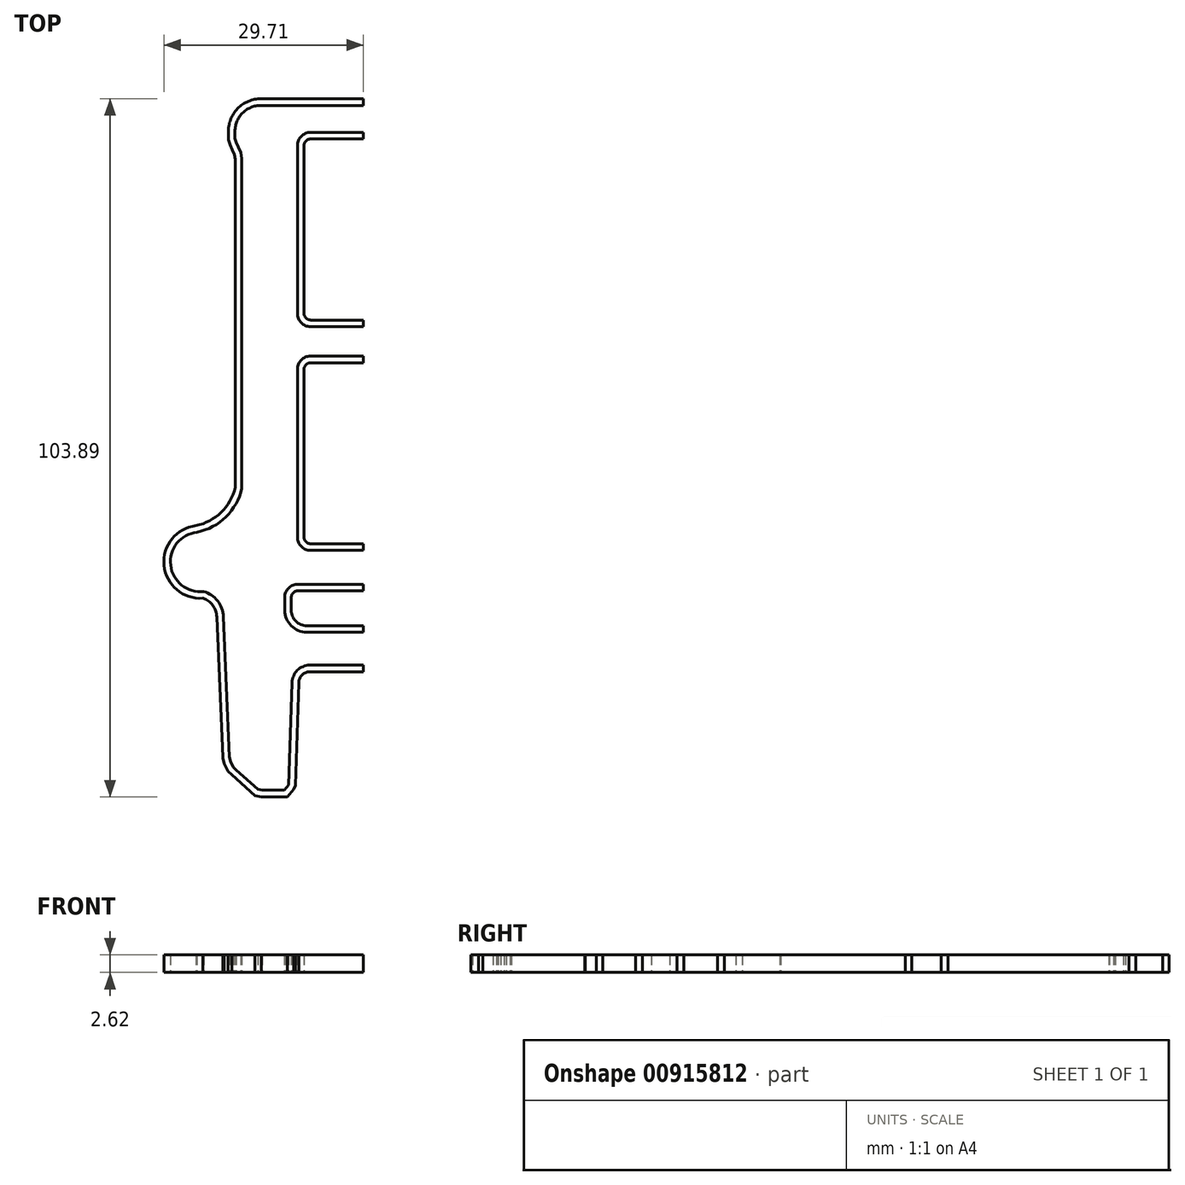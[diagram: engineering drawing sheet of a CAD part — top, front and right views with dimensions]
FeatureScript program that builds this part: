
annotation { "Feature Type Name" : "Feature", "Feature Type Description" : "" }
export const myFeature = defineFeature(function(context is Context, id is Id, definition is map)
    precondition{}
    {
        {
            var Q0;
            Q0=qCreatedBy(makeId("Top.planeOp"),FACE);
            var sketch = newSketch(context, id + "F0", { "sketchPlane" : qUnion([Q0])});
            skLineSegment(sketch, "E0.left", {"start": v(-27.58, 80.06) * mm, "end": v(-27.58, -59.75) * mm});
            skLineSegment(sketch, "E1.bottom", {"start": v(-11.99, 35.27) * mm, "end": v(0, 35.27) * mm});
            skLineSegment(sketch, "E1.top", {"start": v(-11.99, -8.8) * mm, "end": v(0, -8.8) * mm});
            skLineSegment(sketch, "E1.left", {"start": v(-14.99, 32.27) * mm, "end": v(-14.99, -5.8) * mm});
            skPoint(sketch, "E2.visualSharp", {"position": v(-14.99, 36.07) * mm});
            skArc(sketch, "E2.filletArc", {"start": v(-11.99, 35.27) * mm, "mid": v(-14.1, 34.39) * mm, "end": v(-14.99, 32.27) * mm});
            skPoint(sketch, "E3.visualSharp", {"position": v(-14.99, -8.8) * mm});
            skArc(sketch, "E3.filletArc", {"start": v(-14.99, -5.8) * mm, "mid": v(-14.1, -7.92) * mm, "end": v(-11.99, -8.8) * mm});
            skLineSegment(sketch, "E4.bottom", {"start": v(-11.99, 86.01) * mm, "end": v(0, 86.01) * mm});
            skLineSegment(sketch, "E4.top", {"start": v(-11.99, 41.94) * mm, "end": v(0, 41.94) * mm});
            skLineSegment(sketch, "E4.left", {"start": v(-14.99, 83.01) * mm, "end": v(-14.99, 44.94) * mm});
            skPoint(sketch, "E5.visualSharp", {"position": v(-14.99, 86.01) * mm});
            skArc(sketch, "E5.filletArc", {"start": v(-11.99, 86.01) * mm, "mid": v(-14.1, 85.13) * mm, "end": v(-14.99, 83.01) * mm});
            skPoint(sketch, "E6.visualSharp", {"position": v(-14.99, 41.94) * mm});
            skArc(sketch, "E6.filletArc", {"start": v(-14.99, 44.94) * mm, "mid": v(-14.1, 42.82) * mm, "end": v(-11.99, 41.94) * mm});
            skLineSegment(sketch, "E7.bottom", {"start": v(-12.87, -27.38) * mm, "end": v(0, -27.38) * mm});
            skLineSegment(sketch, "E7.top", {"start": v(-14.87, -16.48) * mm, "end": v(0, -16.48) * mm});
            skLineSegment(sketch, "E7.left", {"start": v(-17.87, -22.38) * mm, "end": v(-17.87, -19.48) * mm});
            skPoint(sketch, "E8.visualSharp", {"position": v(-17.87, -16.48) * mm});
            skArc(sketch, "E8.filletArc", {"start": v(-14.87, -16.48) * mm, "mid": v(-16.99, -17.36) * mm, "end": v(-17.87, -19.48) * mm});
            skPoint(sketch, "E9.visualSharp", {"position": v(-17.87, -27.38) * mm});
            skArc(sketch, "E9.filletArc", {"start": v(-17.87, -22.38) * mm, "mid": v(-16.4, -25.92) * mm, "end": v(-12.87, -27.38) * mm});
            skLineSegment(sketch, "E10.bottom", {"start": v(-12.18, -34.84) * mm, "end": v(0, -34.84) * mm});
            skPoint(sketch, "E11.visualSharp", {"position": v(-16.18, -34.84) * mm});
            skArc(sketch, "E11.filletArc", {"start": v(-12.18, -34.84) * mm, "mid": v(-15, -36.01) * mm, "end": v(-16.18, -38.84) * mm});
            skLineSegment(sketch, "E12", {"start": v(-16.18, -38.84) * mm, "end": v(-16.96, -62.01) * mm});
            skLineSegment(sketch, "E13", {"start": v(-16.96, -62.01) * mm, "end": v(-17.99, -63.22) * mm});
            skLineSegment(sketch, "E14", {"start": v(-17.99, -63.22) * mm, "end": v(-23, -63.22) * mm});
            skLineSegment(sketch, "E15", {"start": v(-23, -63.22) * mm, "end": v(-23.9, -63.02) * mm});
            skLineSegment(sketch, "E16", {"start": v(-23.9, -63.02) * mm, "end": v(-28.85, -58.61) * mm});
            skCircle(sketch, "E17", {"center": v(-23.01, -55.13) * mm, "radius": 2.4 * mm});
            skCircle(sketch, "E18", {"center": v(-37, -11.4) * mm, "radius": 6.78 * mm});
            skCircle(sketch, "E19", {"center": v(-37, -11.4) * mm, "radius": 2.4 * mm});
            skLineSegment(sketch, "E20", {"start": v(-31.78, -23.86) * mm, "end": v(-30.39, -55.6) * mm});
            skLineSegment(sketch, "E21", {"start": v(-30.39, -55.6) * mm, "end": v(-30.18, -56.73) * mm});
            skLineSegment(sketch, "E22", {"start": v(-30.18, -56.73) * mm, "end": v(-29.54, -57.98) * mm});
            skLineSegment(sketch, "E23", {"start": v(-29.54, -57.98) * mm, "end": v(-28.85, -58.61) * mm});
            skArc(sketch, "E24", {"start": v(-31.78, -23.86) * mm, "mid": v(-33.08, -20.26) * mm, "end": v(-36.27, -18.14) * mm});
            skArc(sketch, "E25", {"start": v(-37.75, -4.67) * mm, "mid": v(-31.18, -1.2) * mm, "end": v(-27.58, 5.3) * mm});
            skCircle(sketch, "E26", {"center": v(-23.25, 86.23) * mm, "radius": 2.4 * mm});
            skCircle(sketch, "E27", {"center": v(-23.25, 86.23) * mm, "radius": 5.9 * mm});
            skLineSegment(sketch, "E28", {"start": v(-29.15, 86) * mm, "end": v(-29.15, 84.6) * mm});
            skLineSegment(sketch, "E29", {"start": v(-29.15, 84.6) * mm, "end": v(-28.88, 83.73) * mm});
            skLineSegment(sketch, "E30", {"start": v(-28.88, 83.73) * mm, "end": v(-28.4, 82.67) * mm});
            skLineSegment(sketch, "E31", {"start": v(-28.4, 82.67) * mm, "end": v(-27.86, 81.45) * mm});
            skLineSegment(sketch, "E32", {"start": v(-27.86, 81.45) * mm, "end": v(-27.58, 80.06) * mm});
            skLineSegment(sketch, "E33", {"start": v(-23.2, 92.14) * mm, "end": v(0, 92.14) * mm});
            skLineSegment(sketch, "E34.right", {"start": v(0, 92.14) * mm, "end": v(0, 86.01) * mm});
            skLineSegment(sketch, "E35.trimOffspring", {"start": v(0, 41.94) * mm, "end": v(0, 35.27) * mm});
            skLineSegment(sketch, "E36.trimOffspring", {"start": v(0, -8.8) * mm, "end": v(0, -16.48) * mm});
            skLineSegment(sketch, "E37.trimOffspring", {"start": v(0, -27.38) * mm, "end": v(0, -34.84) * mm});
            skLineSegment(sketch, "E38.0", {"start": v(-23.2, 93.64) * mm, "end": v(0, 93.64) * mm});
            skCircle(sketch, "E39.0", {"center": v(-37, -11.4) * mm, "radius": 8.28 * mm});
            skArc(sketch, "E40.0", {"start": v(-38.04, -3.2) * mm, "mid": v(-32.23, -0.12) * mm, "end": v(-29.04, 5.62) * mm});
            skLineSegment(sketch, "E41.0", {"start": v(-29.08, 80.06) * mm, "end": v(-29.08, -59.75) * mm});
            skLineSegment(sketch, "E42.0", {"start": v(-29.3, 80.98) * mm, "end": v(-29.05, 79.76) * mm});
            skLineSegment(sketch, "E42.1", {"start": v(-30.65, 86) * mm, "end": v(-30.65, 84.37) * mm});
            skLineSegment(sketch, "E42.2", {"start": v(-30.65, 84.37) * mm, "end": v(-30.29, 83.2) * mm});
            skLineSegment(sketch, "E42.3", {"start": v(-30.29, 83.2) * mm, "end": v(-29.78, 82.06) * mm});
            skLineSegment(sketch, "E42.4", {"start": v(-29.78, 82.06) * mm, "end": v(-29.3, 80.98) * mm});
            skCircle(sketch, "E43.0", {"center": v(-23.25, 86.23) * mm, "radius": 7.4 * mm});
            skLineSegment(sketch, "E44", {"start": v(0, 93.64) * mm, "end": v(0, 91.95) * mm});
            skLineSegment(sketch, "E45.0", {"start": v(-11.99, 84.51) * mm, "end": v(0, 84.51) * mm});
            skArc(sketch, "E46.0", {"start": v(-11.99, 84.51) * mm, "mid": v(-13.05, 84.07) * mm, "end": v(-13.49, 83.01) * mm});
            skLineSegment(sketch, "E47.0", {"start": v(-13.49, 83.01) * mm, "end": v(-13.49, 44.94) * mm});
            skArc(sketch, "E48.0", {"start": v(-13.49, 44.94) * mm, "mid": v(-13.05, 43.88) * mm, "end": v(-11.99, 43.44) * mm});
            skLineSegment(sketch, "E49.0", {"start": v(-11.99, 43.44) * mm, "end": v(0, 43.44) * mm});
            skLineSegment(sketch, "E50", {"start": v(0, 43.44) * mm, "end": v(0, 41.94) * mm});
            skLineSegment(sketch, "E51.0", {"start": v(-11.99, 33.77) * mm, "end": v(0, 33.77) * mm});
            skArc(sketch, "E52.0", {"start": v(-11.99, 33.77) * mm, "mid": v(-13.05, 33.33) * mm, "end": v(-13.49, 32.27) * mm});
            skLineSegment(sketch, "E53.0", {"start": v(-13.49, 32.27) * mm, "end": v(-13.49, -5.8) * mm});
            skLineSegment(sketch, "E54", {"start": v(0, 35.27) * mm, "end": v(0, 33.77) * mm});
            skArc(sketch, "E55.0", {"start": v(-13.49, -5.8) * mm, "mid": v(-13.05, -6.86) * mm, "end": v(-11.99, -7.3) * mm});
            skLineSegment(sketch, "E56.0", {"start": v(-11.99, -7.3) * mm, "end": v(0, -7.3) * mm});
            skLineSegment(sketch, "E57.0", {"start": v(-14.87, -17.98) * mm, "end": v(0, -17.98) * mm});
            skLineSegment(sketch, "E58", {"start": v(0, -7.3) * mm, "end": v(0, -17.98) * mm});
            skArc(sketch, "E59.0", {"start": v(-14.87, -17.98) * mm, "mid": v(-15.93, -18.42) * mm, "end": v(-16.37, -19.48) * mm});
            skLineSegment(sketch, "E60.0", {"start": v(-16.37, -22.38) * mm, "end": v(-16.37, -19.48) * mm});
            skArc(sketch, "E61.0", {"start": v(-16.37, -22.38) * mm, "mid": v(-15.34, -24.86) * mm, "end": v(-12.87, -25.88) * mm});
            skLineSegment(sketch, "E62.0", {"start": v(-12.87, -25.88) * mm, "end": v(0, -25.88) * mm});
            skLineSegment(sketch, "E63.0", {"start": v(-12.18, -36.34) * mm, "end": v(0, -36.34) * mm});
            skArc(sketch, "E64.0", {"start": v(-12.18, -36.34) * mm, "mid": v(-13.94, -37.07) * mm, "end": v(-14.68, -38.84) * mm});
            skLineSegment(sketch, "E65.0", {"start": v(-14.68, -38.9) * mm, "end": v(-15.46, -62.06) * mm});
            skLineSegment(sketch, "E66.0", {"start": v(-15.82, -62.98) * mm, "end": v(-17.3, -64.72) * mm});
            skLineSegment(sketch, "E66.1", {"start": v(-17.3, -64.72) * mm, "end": v(-23.17, -64.72) * mm});
            skLineSegment(sketch, "E66.2", {"start": v(-23.17, -64.72) * mm, "end": v(-24.61, -64.4) * mm});
            skLineSegment(sketch, "E66.3", {"start": v(-31.86, -55.88) * mm, "end": v(-31.62, -57.21) * mm});
            skLineSegment(sketch, "E66.4", {"start": v(-31.62, -57.21) * mm, "end": v(-30.75, -58.9) * mm});
            skLineSegment(sketch, "E66.5", {"start": v(-30.75, -58.9) * mm, "end": v(-29.85, -59.73) * mm});
            skLineSegment(sketch, "E66.6", {"start": v(-24.61, -64.4) * mm, "end": v(-29.85, -59.73) * mm});
            skLineSegment(sketch, "E67", {"start": v(-15.46, -62.06) * mm, "end": v(-15.82, -62.98) * mm});
            skLineSegment(sketch, "E68.0", {"start": v(-33.27, -23.92) * mm, "end": v(-31.88, -55.67) * mm});
            skLineSegment(sketch, "E69", {"start": v(-31.88, -55.67) * mm, "end": v(-31.86, -55.88) * mm});
            skArc(sketch, "E70.0", {"start": v(-33.27, -23.9) * mm, "mid": v(-34.19, -21.3) * mm, "end": v(-36.42, -19.66) * mm});
            skLineSegment(sketch, "E71", {"start": v(0, 86.01) * mm, "end": v(0, 84.51) * mm});
            skLineSegment(sketch, "E72", {"start": v(0, -25.88) * mm, "end": v(0, -36.34) * mm});
            skLineSegment(sketch, "E73", {"start": v(-14.68, -38.84) * mm, "end": v(-14.68, -38.9) * mm});
            skLineSegment(sketch, "E74", {"start": v(0, -34.84) * mm, "end": v(0, -36.34) * mm});
            skLineSegment(sketch, "E75", {"start": v(-33.27, -23.9) * mm, "end": v(-33.27, -23.92) * mm});
            skSolve(sketch);
        }
        {
            var Q0;
            Q0=makeQuery(id+"F0.imprint","IMPRINT",FACE,{"disambiguationData":[TD([[makeQuery(id+"F0.imprint","IMPRINT",EDGE,{"derivedFrom":sQuery(id+"F0.wireOp",EDGE,"E1.bottom")}),-1.0]])]});
            var Q1;
            {var subQ2=sQuery(id+"F0.wireOp",EDGE,"E7.bottom");Q1=makeQuery(id+"F0.imprint","IMPRINT",FACE,{"disambiguationData":[TD([[makeQuery(id+"F0.imprint","IMPRINT",EDGE,{"derivedFrom":subQ2}),1.0]])]});}
            var Q2;
            {var subQ5=sQuery(id+"F0.wireOp",EDGE,"E38.0");Q2=makeQuery(id+"F0.imprint","IMPRINT",FACE,{"disambiguationData":[TD([[makeQuery(id+"F0.imprint","IMPRINT",EDGE,{"derivedFrom":subQ5}),-1.0]])]});}
            var Q3;
            {var subQ0=sQuery(id+"F0.wireOp",EDGE,"E39.0");var subQ1=sQuery(id+"F0.wireOp",EDGE,"E25");var subQ2=makeQuery(id+"F0.imprint","INTERSECT",VERTEX,{"derivedFrom":[subQ1,subQ0]});Q3=makeQuery(id+"F0.imprint","IMPRINT",FACE,{"disambiguationData":[TD([[makeQuery(id+"F0.imprint","IMPRINT",EDGE,{"disambiguationData":[TD([[subQ2,-1.0]])],"derivedFrom":subQ1}),1.0]])]});}
            var Q4;
            {var subQ0=sQuery(id+"F0.wireOp",EDGE,"E42.2");Q4=makeQuery(id+"F0.imprint","IMPRINT",FACE,{"disambiguationData":[TD([[makeQuery(id+"F0.imprint","IMPRINT",EDGE,{"derivedFrom":subQ0}),1.0]])]});}
            var Q5;
            Q5=makeQuery(id+"F0.imprint","IMPRINT",FACE,{"disambiguationData":[TD([[makeQuery(id+"F0.imprint","IMPRINT",EDGE,{"derivedFrom":sQuery(id+"F0.wireOp",EDGE,"E10.bottom")}),-1.0]])]});
            var Q6;
            {var subQ4=sQuery(id+"F0.wireOp",EDGE,"E24");var subQ5=sQuery(id+"F0.wireOp",EDGE,"E18");var subQ6=makeQuery(id+"F0.imprint","INTERSECT",VERTEX,{"derivedFrom":[subQ5,subQ4]});Q6=makeQuery(id+"F0.imprint","IMPRINT",FACE,{"disambiguationData":[TD([[makeQuery(id+"F0.imprint","IMPRINT",EDGE,{"disambiguationData":[TD([[subQ6,1.0]])],"derivedFrom":subQ5}),-1.0]])]});}
            var Q7;
            {var subQ0=sQuery(id+"F0.wireOp",EDGE,"E28");Q7=makeQuery(id+"F0.imprint","IMPRINT",FACE,{"disambiguationData":[TD([[makeQuery(id+"F0.imprint","IMPRINT",EDGE,{"derivedFrom":subQ0}),-1.0]])]});}
            var Q8;
            Q8=makeQuery(id+"F0.imprint","IMPRINT",FACE,{"disambiguationData":[TD([[makeQuery(id+"F0.imprint","IMPRINT",EDGE,{"derivedFrom":sQuery(id+"F0.wireOp",EDGE,"E4.bottom")}),-1.0]])]});
            extrude(context, id + "F1", {"entities" : qUnion([Q0, Q1, Q2, Q3, Q4, Q5, Q6, Q7, Q8]), "depth" : 4 * mm, "offsetDistance" : 25 * mm});
        }
        {
            var Q0;
            Q0=makeQuery(id+"F1.opExtrude","SWEPT_BODY",BODY,{"disambiguationData":[OSD([sQuery(id+"F0.wireOp",EDGE,"E7.bottom"),sQuery(id+"F0.wireOp",EDGE,"E7.top"),sQuery(id+"F0.wireOp",EDGE,"E7.left"),sQuery(id+"F0.wireOp",EDGE,"E8.filletArc"),sQuery(id+"F0.wireOp",EDGE,"E9.filletArc"),sQuery(id+"F0.wireOp",EDGE,"E57.0"),sQuery(id+"F0.wireOp",EDGE,"E58"),sQuery(id+"F0.wireOp",EDGE,"E59.0"),sQuery(id+"F0.wireOp",EDGE,"E60.0"),sQuery(id+"F0.wireOp",EDGE,"E61.0"),sQuery(id+"F0.wireOp",EDGE,"E62.0"),sQuery(id+"F0.wireOp",EDGE,"E72")])]});
            var Q1;
            Q1=makeQuery(id+"F1.opExtrude","SWEPT_BODY",BODY,{"disambiguationData":[OSD([sQuery(id+"F0.wireOp",EDGE,"E4.bottom"),sQuery(id+"F0.wireOp",EDGE,"E4.top"),sQuery(id+"F0.wireOp",EDGE,"E4.left"),sQuery(id+"F0.wireOp",EDGE,"E5.filletArc"),sQuery(id+"F0.wireOp",EDGE,"E6.filletArc"),sQuery(id+"F0.wireOp",EDGE,"E45.0"),sQuery(id+"F0.wireOp",EDGE,"E46.0"),sQuery(id+"F0.wireOp",EDGE,"E47.0"),sQuery(id+"F0.wireOp",EDGE,"E48.0"),sQuery(id+"F0.wireOp",EDGE,"E49.0"),sQuery(id+"F0.wireOp",EDGE,"E50"),sQuery(id+"F0.wireOp",EDGE,"E71")])]});
            var Q2;
            Q2=makeQuery(id+"F1.opExtrude","SWEPT_BODY",BODY,{"disambiguationData":[OSD([sQuery(id+"F0.wireOp",EDGE,"E1.bottom"),sQuery(id+"F0.wireOp",EDGE,"E1.top"),sQuery(id+"F0.wireOp",EDGE,"E1.left"),sQuery(id+"F0.wireOp",EDGE,"E2.filletArc"),sQuery(id+"F0.wireOp",EDGE,"E3.filletArc"),sQuery(id+"F0.wireOp",EDGE,"E51.0"),sQuery(id+"F0.wireOp",EDGE,"E52.0"),sQuery(id+"F0.wireOp",EDGE,"E53.0"),sQuery(id+"F0.wireOp",EDGE,"E54"),sQuery(id+"F0.wireOp",EDGE,"E55.0"),sQuery(id+"F0.wireOp",EDGE,"E56.0"),sQuery(id+"F0.wireOp",EDGE,"E58")])]});
            var Q3;
            Q3=makeQuery(id+"F1.opExtrude","SWEPT_BODY",BODY,{"disambiguationData":[OSD([sQuery(id+"F0.wireOp",EDGE,"E0.left"),sQuery(id+"F0.wireOp",EDGE,"E10.bottom"),sQuery(id+"F0.wireOp",EDGE,"E11.filletArc"),sQuery(id+"F0.wireOp",EDGE,"E12"),sQuery(id+"F0.wireOp",EDGE,"E13"),sQuery(id+"F0.wireOp",EDGE,"E14"),sQuery(id+"F0.wireOp",EDGE,"E15"),sQuery(id+"F0.wireOp",EDGE,"E16"),sQuery(id+"F0.wireOp",EDGE,"E18"),sQuery(id+"F0.wireOp",EDGE,"E20"),sQuery(id+"F0.wireOp",EDGE,"E21"),sQuery(id+"F0.wireOp",EDGE,"E22"),sQuery(id+"F0.wireOp",EDGE,"E23"),sQuery(id+"F0.wireOp",EDGE,"E24"),sQuery(id+"F0.wireOp",EDGE,"E25"),sQuery(id+"F0.wireOp",EDGE,"E27"),sQuery(id+"F0.wireOp",EDGE,"E28"),sQuery(id+"F0.wireOp",EDGE,"E29"),sQuery(id+"F0.wireOp",EDGE,"E30"),sQuery(id+"F0.wireOp",EDGE,"E31"),sQuery(id+"F0.wireOp",EDGE,"E32"),sQuery(id+"F0.wireOp",EDGE,"E33"),sQuery(id+"F0.wireOp",EDGE,"E38.0"),sQuery(id+"F0.wireOp",EDGE,"E39.0"),sQuery(id+"F0.wireOp",EDGE,"E40.0"),sQuery(id+"F0.wireOp",EDGE,"E41.0"),sQuery(id+"F0.wireOp",EDGE,"E42.0"),sQuery(id+"F0.wireOp",EDGE,"E42.1"),sQuery(id+"F0.wireOp",EDGE,"E42.2"),sQuery(id+"F0.wireOp",EDGE,"E42.3"),sQuery(id+"F0.wireOp",EDGE,"E42.4"),sQuery(id+"F0.wireOp",EDGE,"E43.0"),sQuery(id+"F0.wireOp",EDGE,"E44"),sQuery(id+"F0.wireOp",EDGE,"E63.0"),sQuery(id+"F0.wireOp",EDGE,"E64.0"),sQuery(id+"F0.wireOp",EDGE,"E65.0"),sQuery(id+"F0.wireOp",EDGE,"E66.0"),sQuery(id+"F0.wireOp",EDGE,"E66.1"),sQuery(id+"F0.wireOp",EDGE,"E66.2"),sQuery(id+"F0.wireOp",EDGE,"E66.3"),sQuery(id+"F0.wireOp",EDGE,"E66.4"),sQuery(id+"F0.wireOp",EDGE,"E66.5"),sQuery(id+"F0.wireOp",EDGE,"E66.6"),sQuery(id+"F0.wireOp",EDGE,"E67"),sQuery(id+"F0.wireOp",EDGE,"E68.0"),sQuery(id+"F0.wireOp",EDGE,"E69"),sQuery(id+"F0.wireOp",EDGE,"E70.0"),sQuery(id+"F0.wireOp",EDGE,"E73"),sQuery(id+"F0.wireOp",EDGE,"E74"),sQuery(id+"F0.wireOp",EDGE,"E75")])]});
            var Q4;
            Q4=qCreatedBy(makeId("Origin.pointOp"),VERTEX);
            transform(context, id + "F2", {"entities" : qUnion([Q0, Q1, Q2, Q3]), "transformType" : TransformType.SCALE_UNIFORMLY, "scale" : 0.66, "scalePoint" : qUnion([Q4]), "makeCopy" : false});
        }
    });
